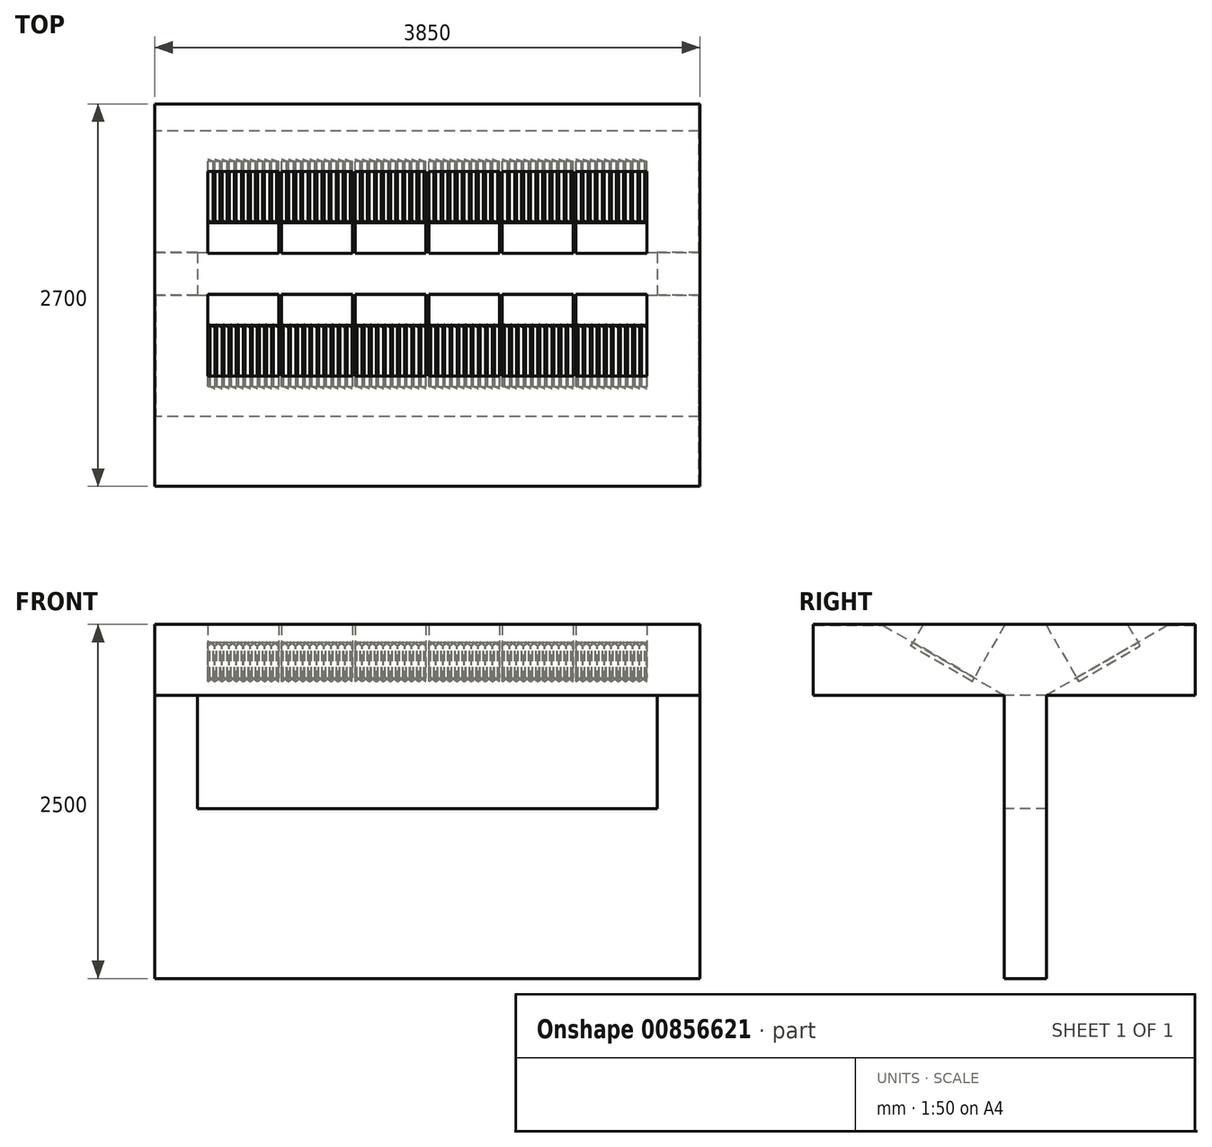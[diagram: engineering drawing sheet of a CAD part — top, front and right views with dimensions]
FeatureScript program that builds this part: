
annotation { "Feature Type Name" : "Feature", "Feature Type Description" : "" }
export const myFeature = defineFeature(function(context is Context, id is Id, definition is map)
    precondition{}
    {
        {
            var Q0;
            Q0=qCreatedBy(makeId("Top.planeOp"),FACE);
            var sketch = newSketch(context, id + "F0", { "sketchPlane" : qUnion([Q0])});
            skLineSegment(sketch, "E0.bottom", {"start": v(0, 0) * mm, "end": v(3850, 0) * mm});
            skLineSegment(sketch, "E0.top", {"start": v(0, -300) * mm, "end": v(3850, -300) * mm});
            skLineSegment(sketch, "E0.left", {"start": v(0, 0) * mm, "end": v(0, -300) * mm});
            skLineSegment(sketch, "E0.right", {"start": v(3850, 0) * mm, "end": v(3850, -300) * mm});
            skSolve(sketch);
        }
        {
            var Q0;
            Q0 = qSketchRegion(id + "F0", true);
            extrude(context, id + "F1", {"entities" : qUnion([Q0]), "depth" : 1200 * mm, "offsetDistance" : 25 * mm});
        }
        {
            var Q0;
            Q0=makeQuery(id+"F1.opExtrude","CAP_FACE",FACE,{"disambiguationData":[OSD([sQuery(id+"F0.wireOp",EDGE,"E0.bottom"),sQuery(id+"F0.wireOp",EDGE,"E0.top"),sQuery(id+"F0.wireOp",EDGE,"E0.left"),sQuery(id+"F0.wireOp",EDGE,"E0.right")])],"isStart":false});
            var sketch = newSketch(context, id + "F2", { "sketchPlane" : qUnion([Q0])});
            skLineSegment(sketch, "E1.bottom", {"start": v(0, 0) * mm, "end": v(300, 0) * mm});
            skLineSegment(sketch, "E1.top", {"start": v(0, -300) * mm, "end": v(300, -300) * mm});
            skLineSegment(sketch, "E1.left", {"start": v(0, 0) * mm, "end": v(0, -300) * mm});
            skLineSegment(sketch, "E1.right", {"start": v(300, 0) * mm, "end": v(300, -300) * mm});
            skLineSegment(sketch, "E2.bottom", {"start": v(3850, 0) * mm, "end": v(3550, 0) * mm});
            skLineSegment(sketch, "E2.top", {"start": v(3850, -300) * mm, "end": v(3550, -300) * mm});
            skLineSegment(sketch, "E2.left", {"start": v(3850, 0) * mm, "end": v(3850, -300) * mm});
            skLineSegment(sketch, "E2.right", {"start": v(3550, 0) * mm, "end": v(3550, -300) * mm});
            skSolve(sketch);
        }
        {
            var Q0;
            Q0 = qSketchRegion(id + "F2", true);
            extrude(context, id + "F3", {"entities" : qUnion([Q0]), "operationType" : NewBodyOperationType.ADD, "depth" : 800 * mm, "offsetDistance" : 25 * mm});
        }
        {
            var Q0;
            Q0=makeQuery(id+"F3.opExtrude","CAP_FACE",FACE,{"disambiguationData":[OSD([sQuery(id+"F2.wireOp",EDGE,"E1.bottom"),sQuery(id+"F2.wireOp",EDGE,"E1.top"),sQuery(id+"F2.wireOp",EDGE,"E1.left"),sQuery(id+"F2.wireOp",EDGE,"E1.right")])],"isStart":false});
            var sketch = newSketch(context, id + "F4", { "sketchPlane" : qUnion([Q0])});
            skLineSegment(sketch, "E3.bottom", {"start": v(0, 1050) * mm, "end": v(3850, 1050) * mm});
            skLineSegment(sketch, "E3.top", {"start": v(0, -1650) * mm, "end": v(3850, -1650) * mm});
            skLineSegment(sketch, "E3.left", {"start": v(0, 1050) * mm, "end": v(0, -1650) * mm});
            skLineSegment(sketch, "E3.right", {"start": v(3850, 1050) * mm, "end": v(3850, -1650) * mm});
            skSolve(sketch);
        }
        {
            var Q0;
            Q0 = qSketchRegion(id + "F4", true);
            extrude(context, id + "F5", {"entities" : qUnion([Q0]), "operationType" : NewBodyOperationType.ADD, "depth" : 500 * mm, "offsetDistance" : 25 * mm});
        }
        {
            var Q0;
            Q0=makeQuery(id+"F5.opExtrude","CAP_FACE",FACE,{"disambiguationData":[OSD([sQuery(id+"F4.wireOp",EDGE,"E3.bottom"),sQuery(id+"F4.wireOp",EDGE,"E3.top"),sQuery(id+"F4.wireOp",EDGE,"E3.left"),sQuery(id+"F4.wireOp",EDGE,"E3.right")])],"isStart":true});
            var sketch = newSketch(context, id + "F6", { "sketchPlane" : qUnion([Q0])});
            skLineSegment(sketch, "E4.bottom", {"start": v(5, 1645) * mm, "end": v(3845, 1645) * mm});
            skLineSegment(sketch, "E4.top", {"start": v(5, 300) * mm, "end": v(3845, 300) * mm});
            skLineSegment(sketch, "E4.left", {"start": v(5, 1645) * mm, "end": v(5, 300) * mm});
            skLineSegment(sketch, "E4.right", {"start": v(3845, 1645) * mm, "end": v(3845, 300) * mm});
            skLineSegment(sketch, "E5.bottom", {"start": v(5, 0) * mm, "end": v(3845, 0) * mm});
            skLineSegment(sketch, "E5.top", {"start": v(5, -1045) * mm, "end": v(3845, -1045) * mm});
            skLineSegment(sketch, "E5.left", {"start": v(5, 0) * mm, "end": v(5, -1045) * mm});
            skLineSegment(sketch, "E5.right", {"start": v(3845, 0) * mm, "end": v(3845, -1045) * mm});
            skSolve(sketch);
        }
        {
            var Q0;
            Q0 = qSketchRegion(id + "F6", true);
            extrude(context, id + "F7", {"entities" : qUnion([Q0]), "operationType" : NewBodyOperationType.REMOVE, "oppositeDirection" : true, "depth" : 495 * mm, "offsetDistance" : 25 * mm});
        }
        {
            var Q0;
            Q0=makeQuery(id+"F7.boolean.opBoolean","COPY",FACE,{"derivedFrom":makeQuery(id+"F7.opExtrude","SWEPT_FACE",FACE,{"disambiguationData":[OSD([sQuery(id+"F6.wireOp",EDGE,"E4.left")])]})});
            var sketch = newSketch(context, id + "F8", { "sketchPlane" : qUnion([Q0])});
            skLineSegment(sketch, "E6", {"start": v(-300, 2000) * mm, "end": v(-1157.37, 2495) * mm});
            skLineSegment(sketch, "E7", {"start": v(-1157.37, 2495) * mm, "end": v(-300, 2495) * mm});
            skLineSegment(sketch, "E8", {"start": v(-300, 2495) * mm, "end": v(-300, 2000) * mm});
            skSolve(sketch);
        }
        {
            var Q0;
            Q0 = qSketchRegion(id + "F8", true);
            extrude(context, id + "F9", {"entities" : qUnion([Q0]), "operationType" : NewBodyOperationType.ADD, "endBound" : BoundingType.UP_TO_NEXT, "depth" : 25 * mm, "offsetDistance" : 25 * mm});
        }
        {
            var Q0;
            Q0=makeQuery(id+"F7.boolean.opBoolean","COPY",FACE,{"derivedFrom":makeQuery(id+"F7.opExtrude","SWEPT_FACE",FACE,{"disambiguationData":[OSD([sQuery(id+"F6.wireOp",EDGE,"E5.left")])]})});
            var sketch = newSketch(context, id + "F10", { "sketchPlane" : qUnion([Q0])});
            skLineSegment(sketch, "E9", {"start": v(0, 2000) * mm, "end": v(857.37, 2495) * mm});
            skLineSegment(sketch, "E10", {"start": v(857.37, 2495) * mm, "end": v(0, 2495) * mm});
            skLineSegment(sketch, "E11", {"start": v(0, 2495) * mm, "end": v(0, 2000) * mm});
            skSolve(sketch);
        }
        {
            var Q0;
            Q0 = qSketchRegion(id + "F10", true);
            extrude(context, id + "F11", {"entities" : qUnion([Q0]), "operationType" : NewBodyOperationType.ADD, "endBound" : BoundingType.UP_TO_NEXT, "depth" : 25 * mm, "offsetDistance" : 25 * mm});
        }
        {
            var Q0;
            Q0=makeQuery(id+"F9.opExtrude","SWEPT_FACE",FACE,{"disambiguationData":[OSD([sQuery(id+"F8.wireOp",EDGE,"E6")])]});
            var sketch = newSketch(context, id + "F12", { "sketchPlane" : qUnion([Q0])});
            skLineSegment(sketch, "E12.bottom", {"start": v(375, 2004.8) * mm, "end": v(875, 2004.8) * mm});
            skLineSegment(sketch, "E12.top", {"start": v(375, 1504.8) * mm, "end": v(875, 1504.8) * mm});
            skLineSegment(sketch, "E12.left", {"start": v(375, 2004.8) * mm, "end": v(375, 1504.8) * mm});
            skLineSegment(sketch, "E12.right", {"start": v(875, 2004.8) * mm, "end": v(875, 1504.8) * mm});
            skLineSegment(sketch, "E13.bottom", {"start": v(895, 2004.8) * mm, "end": v(1395, 2004.8) * mm});
            skLineSegment(sketch, "E13.top", {"start": v(895, 1504.8) * mm, "end": v(1395, 1504.8) * mm});
            skLineSegment(sketch, "E13.left", {"start": v(895, 2004.8) * mm, "end": v(895, 1504.8) * mm});
            skLineSegment(sketch, "E13.right", {"start": v(1395, 2004.8) * mm, "end": v(1395, 1504.8) * mm});
            skLineSegment(sketch, "E14.bottom", {"start": v(1415, 2004.8) * mm, "end": v(1915, 2004.8) * mm});
            skLineSegment(sketch, "E14.top", {"start": v(1415, 1504.8) * mm, "end": v(1915, 1504.8) * mm});
            skLineSegment(sketch, "E14.left", {"start": v(1415, 2004.8) * mm, "end": v(1415, 1504.8) * mm});
            skLineSegment(sketch, "E14.right", {"start": v(1915, 2004.8) * mm, "end": v(1915, 1504.8) * mm});
            skLineSegment(sketch, "E15.bottom", {"start": v(1935, 2004.8) * mm, "end": v(2435, 2004.8) * mm});
            skLineSegment(sketch, "E15.top", {"start": v(1935, 1504.8) * mm, "end": v(2435, 1504.8) * mm});
            skLineSegment(sketch, "E15.left", {"start": v(1935, 2004.8) * mm, "end": v(1935, 1504.8) * mm});
            skLineSegment(sketch, "E15.right", {"start": v(2435, 2004.8) * mm, "end": v(2435, 1504.8) * mm});
            skLineSegment(sketch, "E16.bottom", {"start": v(2455, 2004.8) * mm, "end": v(2955, 2004.8) * mm});
            skLineSegment(sketch, "E16.top", {"start": v(2455, 1504.8) * mm, "end": v(2955, 1504.8) * mm});
            skLineSegment(sketch, "E16.left", {"start": v(2455, 2004.8) * mm, "end": v(2455, 1504.8) * mm});
            skLineSegment(sketch, "E16.right", {"start": v(2955, 2004.8) * mm, "end": v(2955, 1504.8) * mm});
            skLineSegment(sketch, "E17.bottom", {"start": v(2975, 2004.8) * mm, "end": v(3475, 2004.8) * mm});
            skLineSegment(sketch, "E17.top", {"start": v(2975, 1504.8) * mm, "end": v(3475, 1504.8) * mm});
            skLineSegment(sketch, "E17.left", {"start": v(2975, 2004.8) * mm, "end": v(2975, 1504.8) * mm});
            skLineSegment(sketch, "E17.right", {"start": v(3475, 2004.8) * mm, "end": v(3475, 1504.8) * mm});
            skSolve(sketch);
        }
        {
            var Q0;
            Q0 = qSketchRegion(id + "F12", true);
            extrude(context, id + "F13", {"entities" : qUnion([Q0]), "operationType" : NewBodyOperationType.REMOVE, "endBound" : BoundingType.UP_TO_NEXT, "oppositeDirection" : true, "depth" : 25 * mm, "offsetDistance" : 25 * mm});
        }
        {
            var Q0;
            Q0=makeQuery(id+"F11.opExtrude","SWEPT_FACE",FACE,{"disambiguationData":[OSD([sQuery(id+"F10.wireOp",EDGE,"E9")])]});
            var sketch = newSketch(context, id + "F14", { "sketchPlane" : qUnion([Q0])});
            skLineSegment(sketch, "E18.bottom", {"start": v(375, -1245) * mm, "end": v(875, -1245) * mm});
            skLineSegment(sketch, "E18.top", {"start": v(375, -1745) * mm, "end": v(875, -1745) * mm});
            skLineSegment(sketch, "E18.left", {"start": v(375, -1245) * mm, "end": v(375, -1745) * mm});
            skLineSegment(sketch, "E18.right", {"start": v(875, -1245) * mm, "end": v(875, -1745) * mm});
            skLineSegment(sketch, "E19.bottom", {"start": v(895, -1245) * mm, "end": v(1395, -1245) * mm});
            skLineSegment(sketch, "E19.top", {"start": v(895, -1745) * mm, "end": v(1395, -1745) * mm});
            skLineSegment(sketch, "E19.left", {"start": v(895, -1245) * mm, "end": v(895, -1745) * mm});
            skLineSegment(sketch, "E19.right", {"start": v(1395, -1245) * mm, "end": v(1395, -1745) * mm});
            skLineSegment(sketch, "E20.bottom", {"start": v(1415, -1245) * mm, "end": v(1915, -1245) * mm});
            skLineSegment(sketch, "E20.top", {"start": v(1415, -1745) * mm, "end": v(1915, -1745) * mm});
            skLineSegment(sketch, "E20.left", {"start": v(1415, -1245) * mm, "end": v(1415, -1745) * mm});
            skLineSegment(sketch, "E20.right", {"start": v(1915, -1245) * mm, "end": v(1915, -1745) * mm});
            skLineSegment(sketch, "E21.bottom", {"start": v(1935, -1245) * mm, "end": v(2435, -1245) * mm});
            skLineSegment(sketch, "E21.top", {"start": v(1935, -1745) * mm, "end": v(2435, -1745) * mm});
            skLineSegment(sketch, "E21.left", {"start": v(1935, -1245) * mm, "end": v(1935, -1745) * mm});
            skLineSegment(sketch, "E21.right", {"start": v(2435, -1245) * mm, "end": v(2435, -1745) * mm});
            skLineSegment(sketch, "E22.bottom", {"start": v(2455, -1245) * mm, "end": v(2955, -1245) * mm});
            skLineSegment(sketch, "E22.top", {"start": v(2455, -1745) * mm, "end": v(2955, -1745) * mm});
            skLineSegment(sketch, "E22.left", {"start": v(2455, -1245) * mm, "end": v(2455, -1745) * mm});
            skLineSegment(sketch, "E22.right", {"start": v(2955, -1245) * mm, "end": v(2955, -1745) * mm});
            skLineSegment(sketch, "E23.bottom", {"start": v(2975, -1245) * mm, "end": v(3475, -1245) * mm});
            skLineSegment(sketch, "E23.top", {"start": v(2975, -1745) * mm, "end": v(3475, -1745) * mm});
            skLineSegment(sketch, "E23.left", {"start": v(2975, -1245) * mm, "end": v(2975, -1745) * mm});
            skLineSegment(sketch, "E23.right", {"start": v(3475, -1245) * mm, "end": v(3475, -1745) * mm});
            skSolve(sketch);
        }
        {
            var Q0;
            Q0 = qSketchRegion(id + "F14", true);
            extrude(context, id + "F15", {"entities" : qUnion([Q0]), "operationType" : NewBodyOperationType.REMOVE, "endBound" : BoundingType.UP_TO_NEXT, "oppositeDirection" : true, "depth" : 25 * mm, "offsetDistance" : 25 * mm});
        }
        {
            var Q0;
            Q0=makeQuery(id+"F13.boolean.opBoolean","COPY",FACE,{"derivedFrom":makeQuery(id+"F13.opExtrude","SWEPT_FACE",FACE,{"disambiguationData":[OSD([sQuery(id+"F12.wireOp",EDGE,"E12.bottom")])]})});
            var sketch = newSketch(context, id + "F16", { "sketchPlane" : qUnion([Q0])});
            skLineSegment(sketch, "E24", {"start": v(-385, 1584.55) * mm, "end": v(-423.3, 1552.41) * mm});
            skLineSegment(sketch, "E25", {"start": v(-423.3, 1552.41) * mm, "end": v(-424.9, 1554.33) * mm});
            skLineSegment(sketch, "E26", {"start": v(-424.9, 1554.33) * mm, "end": v(-388.89, 1584.55) * mm});
            skLineSegment(sketch, "E27", {"start": v(-388.89, 1584.55) * mm, "end": v(-385, 1584.55) * mm});
            skLineSegment(sketch, "E28.1.0.0", {"start": v(-435, 1584.55) * mm, "end": v(-473.3, 1552.41) * mm});
            skLineSegment(sketch, "E28.1.0.1", {"start": v(-474.9, 1554.33) * mm, "end": v(-438.89, 1584.55) * mm});
            skLineSegment(sketch, "E28.1.0.2", {"start": v(-473.3, 1552.41) * mm, "end": v(-474.9, 1554.33) * mm});
            skLineSegment(sketch, "E28.1.0.3", {"start": v(-438.89, 1584.55) * mm, "end": v(-435, 1584.55) * mm});
            skLineSegment(sketch, "E28.2.0.0", {"start": v(-485, 1584.55) * mm, "end": v(-523.3, 1552.41) * mm});
            skLineSegment(sketch, "E28.2.0.1", {"start": v(-524.9, 1554.33) * mm, "end": v(-488.89, 1584.55) * mm});
            skLineSegment(sketch, "E28.2.0.2", {"start": v(-523.3, 1552.41) * mm, "end": v(-524.9, 1554.33) * mm});
            skLineSegment(sketch, "E28.2.0.3", {"start": v(-488.89, 1584.55) * mm, "end": v(-485, 1584.55) * mm});
            skLineSegment(sketch, "E28.3.0.0", {"start": v(-535, 1584.55) * mm, "end": v(-573.3, 1552.41) * mm});
            skLineSegment(sketch, "E28.3.0.1", {"start": v(-574.9, 1554.33) * mm, "end": v(-538.89, 1584.55) * mm});
            skLineSegment(sketch, "E28.3.0.2", {"start": v(-573.3, 1552.41) * mm, "end": v(-574.9, 1554.33) * mm});
            skLineSegment(sketch, "E28.3.0.3", {"start": v(-538.89, 1584.55) * mm, "end": v(-535, 1584.55) * mm});
            skLineSegment(sketch, "E28.4.0.0", {"start": v(-585, 1584.55) * mm, "end": v(-623.3, 1552.41) * mm});
            skLineSegment(sketch, "E28.4.0.1", {"start": v(-624.9, 1554.33) * mm, "end": v(-588.89, 1584.55) * mm});
            skLineSegment(sketch, "E28.4.0.2", {"start": v(-623.3, 1552.41) * mm, "end": v(-624.9, 1554.33) * mm});
            skLineSegment(sketch, "E28.4.0.3", {"start": v(-588.89, 1584.55) * mm, "end": v(-585, 1584.55) * mm});
            skLineSegment(sketch, "E28.5.0.0", {"start": v(-635, 1584.55) * mm, "end": v(-673.3, 1552.41) * mm});
            skLineSegment(sketch, "E28.5.0.1", {"start": v(-674.9, 1554.33) * mm, "end": v(-638.89, 1584.55) * mm});
            skLineSegment(sketch, "E28.5.0.2", {"start": v(-673.3, 1552.41) * mm, "end": v(-674.9, 1554.33) * mm});
            skLineSegment(sketch, "E28.5.0.3", {"start": v(-638.89, 1584.55) * mm, "end": v(-635, 1584.55) * mm});
            skLineSegment(sketch, "E28.6.0.0", {"start": v(-685, 1584.55) * mm, "end": v(-723.3, 1552.41) * mm});
            skLineSegment(sketch, "E28.6.0.1", {"start": v(-724.9, 1554.33) * mm, "end": v(-688.89, 1584.55) * mm});
            skLineSegment(sketch, "E28.6.0.2", {"start": v(-723.3, 1552.41) * mm, "end": v(-724.9, 1554.33) * mm});
            skLineSegment(sketch, "E28.6.0.3", {"start": v(-688.89, 1584.55) * mm, "end": v(-685, 1584.55) * mm});
            skLineSegment(sketch, "E28.7.0.0", {"start": v(-735, 1584.55) * mm, "end": v(-773.3, 1552.41) * mm});
            skLineSegment(sketch, "E28.7.0.1", {"start": v(-774.9, 1554.33) * mm, "end": v(-738.89, 1584.55) * mm});
            skLineSegment(sketch, "E28.7.0.2", {"start": v(-773.3, 1552.41) * mm, "end": v(-774.9, 1554.33) * mm});
            skLineSegment(sketch, "E28.7.0.3", {"start": v(-738.89, 1584.55) * mm, "end": v(-735, 1584.55) * mm});
            skLineSegment(sketch, "E28.8.0.0", {"start": v(-785, 1584.55) * mm, "end": v(-823.3, 1552.41) * mm});
            skLineSegment(sketch, "E28.8.0.1", {"start": v(-824.9, 1554.33) * mm, "end": v(-788.89, 1584.55) * mm});
            skLineSegment(sketch, "E28.8.0.2", {"start": v(-823.3, 1552.41) * mm, "end": v(-824.9, 1554.33) * mm});
            skLineSegment(sketch, "E28.8.0.3", {"start": v(-788.89, 1584.55) * mm, "end": v(-785, 1584.55) * mm});
            skLineSegment(sketch, "E28.9.0.0", {"start": v(-835, 1584.55) * mm, "end": v(-873.3, 1552.41) * mm});
            skLineSegment(sketch, "E28.9.0.1", {"start": v(-874.9, 1554.33) * mm, "end": v(-838.89, 1584.55) * mm});
            skLineSegment(sketch, "E28.9.0.2", {"start": v(-873.3, 1552.41) * mm, "end": v(-874.9, 1554.33) * mm});
            skLineSegment(sketch, "E28.9.0.3", {"start": v(-838.89, 1584.55) * mm, "end": v(-835, 1584.55) * mm});
            skLineSegment(sketch, "E28.direction1", {"start": v(-423.3, 1552.41) * mm, "end": v(-473.3, 1552.41) * mm, "construction": true});
            skLineSegment(sketch, "E29.1.0.0", {"start": v(-944.9, 1554.33) * mm, "end": v(-908.89, 1584.55) * mm});
            skLineSegment(sketch, "E29.1.0.1", {"start": v(-905, 1584.55) * mm, "end": v(-943.3, 1552.41) * mm});
            skLineSegment(sketch, "E29.1.0.2", {"start": v(-1394.9, 1554.33) * mm, "end": v(-1358.89, 1584.55) * mm});
            skLineSegment(sketch, "E29.1.0.3", {"start": v(-1194.9, 1554.33) * mm, "end": v(-1158.89, 1584.55) * mm});
            skLineSegment(sketch, "E29.1.0.4", {"start": v(-955, 1584.55) * mm, "end": v(-993.3, 1552.41) * mm});
            skLineSegment(sketch, "E29.1.0.5", {"start": v(-1355, 1584.55) * mm, "end": v(-1393.3, 1552.41) * mm});
            skLineSegment(sketch, "E29.1.0.6", {"start": v(-1294.9, 1554.33) * mm, "end": v(-1258.89, 1584.55) * mm});
            skLineSegment(sketch, "E29.1.0.7", {"start": v(-1155, 1584.55) * mm, "end": v(-1193.3, 1552.41) * mm});
            skLineSegment(sketch, "E29.1.0.8", {"start": v(-994.9, 1554.33) * mm, "end": v(-958.89, 1584.55) * mm});
            skLineSegment(sketch, "E29.1.0.9", {"start": v(-1344.9, 1554.33) * mm, "end": v(-1308.89, 1584.55) * mm});
            skLineSegment(sketch, "E29.1.0.10", {"start": v(-1144.9, 1554.33) * mm, "end": v(-1108.89, 1584.55) * mm});
            skLineSegment(sketch, "E29.1.0.11", {"start": v(-1305, 1584.55) * mm, "end": v(-1343.3, 1552.41) * mm});
            skLineSegment(sketch, "E29.1.0.12", {"start": v(-1105, 1584.55) * mm, "end": v(-1143.3, 1552.41) * mm});
            skLineSegment(sketch, "E29.1.0.13", {"start": v(-1005, 1584.55) * mm, "end": v(-1043.3, 1552.41) * mm});
            skLineSegment(sketch, "E29.1.0.14", {"start": v(-1255, 1584.55) * mm, "end": v(-1293.3, 1552.41) * mm});
            skLineSegment(sketch, "E29.1.0.15", {"start": v(-1044.9, 1554.33) * mm, "end": v(-1008.89, 1584.55) * mm});
            skLineSegment(sketch, "E29.1.0.16", {"start": v(-1094.9, 1554.33) * mm, "end": v(-1058.89, 1584.55) * mm});
            skLineSegment(sketch, "E29.1.0.17", {"start": v(-1244.9, 1554.33) * mm, "end": v(-1208.89, 1584.55) * mm});
            skLineSegment(sketch, "E29.1.0.18", {"start": v(-1055, 1584.55) * mm, "end": v(-1093.3, 1552.41) * mm});
            skLineSegment(sketch, "E29.1.0.19", {"start": v(-943.3, 1552.41) * mm, "end": v(-993.3, 1552.41) * mm, "construction": true});
            skLineSegment(sketch, "E29.1.0.20", {"start": v(-1205, 1584.55) * mm, "end": v(-1243.3, 1552.41) * mm});
            skLineSegment(sketch, "E29.1.0.21", {"start": v(-1393.3, 1552.41) * mm, "end": v(-1394.9, 1554.33) * mm});
            skLineSegment(sketch, "E29.1.0.22", {"start": v(-1193.3, 1552.41) * mm, "end": v(-1194.9, 1554.33) * mm});
            skLineSegment(sketch, "E29.1.0.23", {"start": v(-908.89, 1584.55) * mm, "end": v(-905, 1584.55) * mm});
            skLineSegment(sketch, "E29.1.0.24", {"start": v(-1293.3, 1552.41) * mm, "end": v(-1294.9, 1554.33) * mm});
            skLineSegment(sketch, "E29.1.0.25", {"start": v(-1258.89, 1584.55) * mm, "end": v(-1255, 1584.55) * mm});
            skLineSegment(sketch, "E29.1.0.26", {"start": v(-1308.89, 1584.55) * mm, "end": v(-1305, 1584.55) * mm});
            skLineSegment(sketch, "E29.1.0.27", {"start": v(-1108.89, 1584.55) * mm, "end": v(-1105, 1584.55) * mm});
            skLineSegment(sketch, "E29.1.0.28", {"start": v(-1343.3, 1552.41) * mm, "end": v(-1344.9, 1554.33) * mm});
            skLineSegment(sketch, "E29.1.0.29", {"start": v(-1143.3, 1552.41) * mm, "end": v(-1144.9, 1554.33) * mm});
            skLineSegment(sketch, "E29.1.0.30", {"start": v(-958.89, 1584.55) * mm, "end": v(-955, 1584.55) * mm});
            skLineSegment(sketch, "E29.1.0.31", {"start": v(-1208.89, 1584.55) * mm, "end": v(-1205, 1584.55) * mm});
            skLineSegment(sketch, "E29.1.0.32", {"start": v(-1058.89, 1584.55) * mm, "end": v(-1055, 1584.55) * mm});
            skLineSegment(sketch, "E29.1.0.33", {"start": v(-1043.3, 1552.41) * mm, "end": v(-1044.9, 1554.33) * mm});
            skLineSegment(sketch, "E29.1.0.34", {"start": v(-1243.3, 1552.41) * mm, "end": v(-1244.9, 1554.33) * mm});
            skLineSegment(sketch, "E29.1.0.35", {"start": v(-1008.89, 1584.55) * mm, "end": v(-1005, 1584.55) * mm});
            skLineSegment(sketch, "E29.1.0.36", {"start": v(-1093.3, 1552.41) * mm, "end": v(-1094.9, 1554.33) * mm});
            skLineSegment(sketch, "E29.1.0.37", {"start": v(-1358.89, 1584.55) * mm, "end": v(-1355, 1584.55) * mm});
            skLineSegment(sketch, "E29.1.0.38", {"start": v(-1158.89, 1584.55) * mm, "end": v(-1155, 1584.55) * mm});
            skLineSegment(sketch, "E29.1.0.39", {"start": v(-943.3, 1552.41) * mm, "end": v(-944.9, 1554.33) * mm});
            skLineSegment(sketch, "E29.1.0.40", {"start": v(-993.3, 1552.41) * mm, "end": v(-994.9, 1554.33) * mm});
            skLineSegment(sketch, "E29.2.0.0", {"start": v(-1464.9, 1554.33) * mm, "end": v(-1428.89, 1584.55) * mm});
            skLineSegment(sketch, "E29.2.0.1", {"start": v(-1425, 1584.55) * mm, "end": v(-1463.3, 1552.41) * mm});
            skLineSegment(sketch, "E29.2.0.2", {"start": v(-1914.9, 1554.33) * mm, "end": v(-1878.89, 1584.55) * mm});
            skLineSegment(sketch, "E29.2.0.3", {"start": v(-1714.9, 1554.33) * mm, "end": v(-1678.89, 1584.55) * mm});
            skLineSegment(sketch, "E29.2.0.4", {"start": v(-1475, 1584.55) * mm, "end": v(-1513.3, 1552.41) * mm});
            skLineSegment(sketch, "E29.2.0.5", {"start": v(-1875, 1584.55) * mm, "end": v(-1913.3, 1552.41) * mm});
            skLineSegment(sketch, "E29.2.0.6", {"start": v(-1814.9, 1554.33) * mm, "end": v(-1778.89, 1584.55) * mm});
            skLineSegment(sketch, "E29.2.0.7", {"start": v(-1675, 1584.55) * mm, "end": v(-1713.3, 1552.41) * mm});
            skLineSegment(sketch, "E29.2.0.8", {"start": v(-1514.9, 1554.33) * mm, "end": v(-1478.89, 1584.55) * mm});
            skLineSegment(sketch, "E29.2.0.9", {"start": v(-1864.9, 1554.33) * mm, "end": v(-1828.89, 1584.55) * mm});
            skLineSegment(sketch, "E29.2.0.10", {"start": v(-1664.9, 1554.33) * mm, "end": v(-1628.89, 1584.55) * mm});
            skLineSegment(sketch, "E29.2.0.11", {"start": v(-1825, 1584.55) * mm, "end": v(-1863.3, 1552.41) * mm});
            skLineSegment(sketch, "E29.2.0.12", {"start": v(-1625, 1584.55) * mm, "end": v(-1663.3, 1552.41) * mm});
            skLineSegment(sketch, "E29.2.0.13", {"start": v(-1525, 1584.55) * mm, "end": v(-1563.3, 1552.41) * mm});
            skLineSegment(sketch, "E29.2.0.14", {"start": v(-1775, 1584.55) * mm, "end": v(-1813.3, 1552.41) * mm});
            skLineSegment(sketch, "E29.2.0.15", {"start": v(-1564.9, 1554.33) * mm, "end": v(-1528.89, 1584.55) * mm});
            skLineSegment(sketch, "E29.2.0.16", {"start": v(-1614.9, 1554.33) * mm, "end": v(-1578.89, 1584.55) * mm});
            skLineSegment(sketch, "E29.2.0.17", {"start": v(-1764.9, 1554.33) * mm, "end": v(-1728.89, 1584.55) * mm});
            skLineSegment(sketch, "E29.2.0.18", {"start": v(-1575, 1584.55) * mm, "end": v(-1613.3, 1552.41) * mm});
            skLineSegment(sketch, "E29.2.0.19", {"start": v(-1463.3, 1552.41) * mm, "end": v(-1513.3, 1552.41) * mm, "construction": true});
            skLineSegment(sketch, "E29.2.0.20", {"start": v(-1725, 1584.55) * mm, "end": v(-1763.3, 1552.41) * mm});
            skLineSegment(sketch, "E29.2.0.21", {"start": v(-1913.3, 1552.41) * mm, "end": v(-1914.9, 1554.33) * mm});
            skLineSegment(sketch, "E29.2.0.22", {"start": v(-1713.3, 1552.41) * mm, "end": v(-1714.9, 1554.33) * mm});
            skLineSegment(sketch, "E29.2.0.23", {"start": v(-1428.89, 1584.55) * mm, "end": v(-1425, 1584.55) * mm});
            skLineSegment(sketch, "E29.2.0.24", {"start": v(-1813.3, 1552.41) * mm, "end": v(-1814.9, 1554.33) * mm});
            skLineSegment(sketch, "E29.2.0.25", {"start": v(-1778.89, 1584.55) * mm, "end": v(-1775, 1584.55) * mm});
            skLineSegment(sketch, "E29.2.0.26", {"start": v(-1828.89, 1584.55) * mm, "end": v(-1825, 1584.55) * mm});
            skLineSegment(sketch, "E29.2.0.27", {"start": v(-1628.89, 1584.55) * mm, "end": v(-1625, 1584.55) * mm});
            skLineSegment(sketch, "E29.2.0.28", {"start": v(-1863.3, 1552.41) * mm, "end": v(-1864.9, 1554.33) * mm});
            skLineSegment(sketch, "E29.2.0.29", {"start": v(-1663.3, 1552.41) * mm, "end": v(-1664.9, 1554.33) * mm});
            skLineSegment(sketch, "E29.2.0.30", {"start": v(-1478.89, 1584.55) * mm, "end": v(-1475, 1584.55) * mm});
            skLineSegment(sketch, "E29.2.0.31", {"start": v(-1728.89, 1584.55) * mm, "end": v(-1725, 1584.55) * mm});
            skLineSegment(sketch, "E29.2.0.32", {"start": v(-1578.89, 1584.55) * mm, "end": v(-1575, 1584.55) * mm});
            skLineSegment(sketch, "E29.2.0.33", {"start": v(-1563.3, 1552.41) * mm, "end": v(-1564.9, 1554.33) * mm});
            skLineSegment(sketch, "E29.2.0.34", {"start": v(-1763.3, 1552.41) * mm, "end": v(-1764.9, 1554.33) * mm});
            skLineSegment(sketch, "E29.2.0.35", {"start": v(-1528.89, 1584.55) * mm, "end": v(-1525, 1584.55) * mm});
            skLineSegment(sketch, "E29.2.0.36", {"start": v(-1613.3, 1552.41) * mm, "end": v(-1614.9, 1554.33) * mm});
            skLineSegment(sketch, "E29.2.0.37", {"start": v(-1878.89, 1584.55) * mm, "end": v(-1875, 1584.55) * mm});
            skLineSegment(sketch, "E29.2.0.38", {"start": v(-1678.89, 1584.55) * mm, "end": v(-1675, 1584.55) * mm});
            skLineSegment(sketch, "E29.2.0.39", {"start": v(-1463.3, 1552.41) * mm, "end": v(-1464.9, 1554.33) * mm});
            skLineSegment(sketch, "E29.2.0.40", {"start": v(-1513.3, 1552.41) * mm, "end": v(-1514.9, 1554.33) * mm});
            skLineSegment(sketch, "E29.3.0.0", {"start": v(-1984.9, 1554.33) * mm, "end": v(-1948.89, 1584.55) * mm});
            skLineSegment(sketch, "E29.3.0.1", {"start": v(-1945, 1584.55) * mm, "end": v(-1983.3, 1552.41) * mm});
            skLineSegment(sketch, "E29.3.0.2", {"start": v(-2434.9, 1554.33) * mm, "end": v(-2398.89, 1584.55) * mm});
            skLineSegment(sketch, "E29.3.0.3", {"start": v(-2234.9, 1554.33) * mm, "end": v(-2198.89, 1584.55) * mm});
            skLineSegment(sketch, "E29.3.0.4", {"start": v(-1995, 1584.55) * mm, "end": v(-2033.3, 1552.41) * mm});
            skLineSegment(sketch, "E29.3.0.5", {"start": v(-2395, 1584.55) * mm, "end": v(-2433.3, 1552.41) * mm});
            skLineSegment(sketch, "E29.3.0.6", {"start": v(-2334.9, 1554.33) * mm, "end": v(-2298.89, 1584.55) * mm});
            skLineSegment(sketch, "E29.3.0.7", {"start": v(-2195, 1584.55) * mm, "end": v(-2233.3, 1552.41) * mm});
            skLineSegment(sketch, "E29.3.0.8", {"start": v(-2034.9, 1554.33) * mm, "end": v(-1998.89, 1584.55) * mm});
            skLineSegment(sketch, "E29.3.0.9", {"start": v(-2384.9, 1554.33) * mm, "end": v(-2348.89, 1584.55) * mm});
            skLineSegment(sketch, "E29.3.0.10", {"start": v(-2184.9, 1554.33) * mm, "end": v(-2148.89, 1584.55) * mm});
            skLineSegment(sketch, "E29.3.0.11", {"start": v(-2345, 1584.55) * mm, "end": v(-2383.3, 1552.41) * mm});
            skLineSegment(sketch, "E29.3.0.12", {"start": v(-2145, 1584.55) * mm, "end": v(-2183.3, 1552.41) * mm});
            skLineSegment(sketch, "E29.3.0.13", {"start": v(-2045, 1584.55) * mm, "end": v(-2083.3, 1552.41) * mm});
            skLineSegment(sketch, "E29.3.0.14", {"start": v(-2295, 1584.55) * mm, "end": v(-2333.3, 1552.41) * mm});
            skLineSegment(sketch, "E29.3.0.15", {"start": v(-2084.9, 1554.33) * mm, "end": v(-2048.89, 1584.55) * mm});
            skLineSegment(sketch, "E29.3.0.16", {"start": v(-2134.9, 1554.33) * mm, "end": v(-2098.89, 1584.55) * mm});
            skLineSegment(sketch, "E29.3.0.17", {"start": v(-2284.9, 1554.33) * mm, "end": v(-2248.89, 1584.55) * mm});
            skLineSegment(sketch, "E29.3.0.18", {"start": v(-2095, 1584.55) * mm, "end": v(-2133.3, 1552.41) * mm});
            skLineSegment(sketch, "E29.3.0.19", {"start": v(-1983.3, 1552.41) * mm, "end": v(-2033.3, 1552.41) * mm, "construction": true});
            skLineSegment(sketch, "E29.3.0.20", {"start": v(-2245, 1584.55) * mm, "end": v(-2283.3, 1552.41) * mm});
            skLineSegment(sketch, "E29.3.0.21", {"start": v(-2433.3, 1552.41) * mm, "end": v(-2434.9, 1554.33) * mm});
            skLineSegment(sketch, "E29.3.0.22", {"start": v(-2233.3, 1552.41) * mm, "end": v(-2234.9, 1554.33) * mm});
            skLineSegment(sketch, "E29.3.0.23", {"start": v(-1948.89, 1584.55) * mm, "end": v(-1945, 1584.55) * mm});
            skLineSegment(sketch, "E29.3.0.24", {"start": v(-2333.3, 1552.41) * mm, "end": v(-2334.9, 1554.33) * mm});
            skLineSegment(sketch, "E29.3.0.25", {"start": v(-2298.89, 1584.55) * mm, "end": v(-2295, 1584.55) * mm});
            skLineSegment(sketch, "E29.3.0.26", {"start": v(-2348.89, 1584.55) * mm, "end": v(-2345, 1584.55) * mm});
            skLineSegment(sketch, "E29.3.0.27", {"start": v(-2148.89, 1584.55) * mm, "end": v(-2145, 1584.55) * mm});
            skLineSegment(sketch, "E29.3.0.28", {"start": v(-2383.3, 1552.41) * mm, "end": v(-2384.9, 1554.33) * mm});
            skLineSegment(sketch, "E29.3.0.29", {"start": v(-2183.3, 1552.41) * mm, "end": v(-2184.9, 1554.33) * mm});
            skLineSegment(sketch, "E29.3.0.30", {"start": v(-1998.89, 1584.55) * mm, "end": v(-1995, 1584.55) * mm});
            skLineSegment(sketch, "E29.3.0.31", {"start": v(-2248.89, 1584.55) * mm, "end": v(-2245, 1584.55) * mm});
            skLineSegment(sketch, "E29.3.0.32", {"start": v(-2098.89, 1584.55) * mm, "end": v(-2095, 1584.55) * mm});
            skLineSegment(sketch, "E29.3.0.33", {"start": v(-2083.3, 1552.41) * mm, "end": v(-2084.9, 1554.33) * mm});
            skLineSegment(sketch, "E29.3.0.34", {"start": v(-2283.3, 1552.41) * mm, "end": v(-2284.9, 1554.33) * mm});
            skLineSegment(sketch, "E29.3.0.35", {"start": v(-2048.89, 1584.55) * mm, "end": v(-2045, 1584.55) * mm});
            skLineSegment(sketch, "E29.3.0.36", {"start": v(-2133.3, 1552.41) * mm, "end": v(-2134.9, 1554.33) * mm});
            skLineSegment(sketch, "E29.3.0.37", {"start": v(-2398.89, 1584.55) * mm, "end": v(-2395, 1584.55) * mm});
            skLineSegment(sketch, "E29.3.0.38", {"start": v(-2198.89, 1584.55) * mm, "end": v(-2195, 1584.55) * mm});
            skLineSegment(sketch, "E29.3.0.39", {"start": v(-1983.3, 1552.41) * mm, "end": v(-1984.9, 1554.33) * mm});
            skLineSegment(sketch, "E29.3.0.40", {"start": v(-2033.3, 1552.41) * mm, "end": v(-2034.9, 1554.33) * mm});
            skLineSegment(sketch, "E29.4.0.0", {"start": v(-2504.9, 1554.33) * mm, "end": v(-2468.89, 1584.55) * mm});
            skLineSegment(sketch, "E29.4.0.1", {"start": v(-2465, 1584.55) * mm, "end": v(-2503.3, 1552.41) * mm});
            skLineSegment(sketch, "E29.4.0.2", {"start": v(-2954.9, 1554.33) * mm, "end": v(-2918.89, 1584.55) * mm});
            skLineSegment(sketch, "E29.4.0.3", {"start": v(-2754.9, 1554.33) * mm, "end": v(-2718.89, 1584.55) * mm});
            skLineSegment(sketch, "E29.4.0.4", {"start": v(-2515, 1584.55) * mm, "end": v(-2553.3, 1552.41) * mm});
            skLineSegment(sketch, "E29.4.0.5", {"start": v(-2915, 1584.55) * mm, "end": v(-2953.3, 1552.41) * mm});
            skLineSegment(sketch, "E29.4.0.6", {"start": v(-2854.9, 1554.33) * mm, "end": v(-2818.89, 1584.55) * mm});
            skLineSegment(sketch, "E29.4.0.7", {"start": v(-2715, 1584.55) * mm, "end": v(-2753.3, 1552.41) * mm});
            skLineSegment(sketch, "E29.4.0.8", {"start": v(-2554.9, 1554.33) * mm, "end": v(-2518.89, 1584.55) * mm});
            skLineSegment(sketch, "E29.4.0.9", {"start": v(-2904.9, 1554.33) * mm, "end": v(-2868.89, 1584.55) * mm});
            skLineSegment(sketch, "E29.4.0.10", {"start": v(-2704.9, 1554.33) * mm, "end": v(-2668.89, 1584.55) * mm});
            skLineSegment(sketch, "E29.4.0.11", {"start": v(-2865, 1584.55) * mm, "end": v(-2903.3, 1552.41) * mm});
            skLineSegment(sketch, "E29.4.0.12", {"start": v(-2665, 1584.55) * mm, "end": v(-2703.3, 1552.41) * mm});
            skLineSegment(sketch, "E29.4.0.13", {"start": v(-2565, 1584.55) * mm, "end": v(-2603.3, 1552.41) * mm});
            skLineSegment(sketch, "E29.4.0.14", {"start": v(-2815, 1584.55) * mm, "end": v(-2853.3, 1552.41) * mm});
            skLineSegment(sketch, "E29.4.0.15", {"start": v(-2604.9, 1554.33) * mm, "end": v(-2568.89, 1584.55) * mm});
            skLineSegment(sketch, "E29.4.0.16", {"start": v(-2654.9, 1554.33) * mm, "end": v(-2618.89, 1584.55) * mm});
            skLineSegment(sketch, "E29.4.0.17", {"start": v(-2804.9, 1554.33) * mm, "end": v(-2768.89, 1584.55) * mm});
            skLineSegment(sketch, "E29.4.0.18", {"start": v(-2615, 1584.55) * mm, "end": v(-2653.3, 1552.41) * mm});
            skLineSegment(sketch, "E29.4.0.19", {"start": v(-2503.3, 1552.41) * mm, "end": v(-2553.3, 1552.41) * mm, "construction": true});
            skLineSegment(sketch, "E29.4.0.20", {"start": v(-2765, 1584.55) * mm, "end": v(-2803.3, 1552.41) * mm});
            skLineSegment(sketch, "E29.4.0.21", {"start": v(-2953.3, 1552.41) * mm, "end": v(-2954.9, 1554.33) * mm});
            skLineSegment(sketch, "E29.4.0.22", {"start": v(-2753.3, 1552.41) * mm, "end": v(-2754.9, 1554.33) * mm});
            skLineSegment(sketch, "E29.4.0.23", {"start": v(-2468.89, 1584.55) * mm, "end": v(-2465, 1584.55) * mm});
            skLineSegment(sketch, "E29.4.0.24", {"start": v(-2853.3, 1552.41) * mm, "end": v(-2854.9, 1554.33) * mm});
            skLineSegment(sketch, "E29.4.0.25", {"start": v(-2818.89, 1584.55) * mm, "end": v(-2815, 1584.55) * mm});
            skLineSegment(sketch, "E29.4.0.26", {"start": v(-2868.89, 1584.55) * mm, "end": v(-2865, 1584.55) * mm});
            skLineSegment(sketch, "E29.4.0.27", {"start": v(-2668.89, 1584.55) * mm, "end": v(-2665, 1584.55) * mm});
            skLineSegment(sketch, "E29.4.0.28", {"start": v(-2903.3, 1552.41) * mm, "end": v(-2904.9, 1554.33) * mm});
            skLineSegment(sketch, "E29.4.0.29", {"start": v(-2703.3, 1552.41) * mm, "end": v(-2704.9, 1554.33) * mm});
            skLineSegment(sketch, "E29.4.0.30", {"start": v(-2518.89, 1584.55) * mm, "end": v(-2515, 1584.55) * mm});
            skLineSegment(sketch, "E29.4.0.31", {"start": v(-2768.89, 1584.55) * mm, "end": v(-2765, 1584.55) * mm});
            skLineSegment(sketch, "E29.4.0.32", {"start": v(-2618.89, 1584.55) * mm, "end": v(-2615, 1584.55) * mm});
            skLineSegment(sketch, "E29.4.0.33", {"start": v(-2603.3, 1552.41) * mm, "end": v(-2604.9, 1554.33) * mm});
            skLineSegment(sketch, "E29.4.0.34", {"start": v(-2803.3, 1552.41) * mm, "end": v(-2804.9, 1554.33) * mm});
            skLineSegment(sketch, "E29.4.0.35", {"start": v(-2568.89, 1584.55) * mm, "end": v(-2565, 1584.55) * mm});
            skLineSegment(sketch, "E29.4.0.36", {"start": v(-2653.3, 1552.41) * mm, "end": v(-2654.9, 1554.33) * mm});
            skLineSegment(sketch, "E29.4.0.37", {"start": v(-2918.89, 1584.55) * mm, "end": v(-2915, 1584.55) * mm});
            skLineSegment(sketch, "E29.4.0.38", {"start": v(-2718.89, 1584.55) * mm, "end": v(-2715, 1584.55) * mm});
            skLineSegment(sketch, "E29.4.0.39", {"start": v(-2503.3, 1552.41) * mm, "end": v(-2504.9, 1554.33) * mm});
            skLineSegment(sketch, "E29.4.0.40", {"start": v(-2553.3, 1552.41) * mm, "end": v(-2554.9, 1554.33) * mm});
            skLineSegment(sketch, "E29.5.0.0", {"start": v(-3024.9, 1554.33) * mm, "end": v(-2988.89, 1584.55) * mm});
            skLineSegment(sketch, "E29.5.0.1", {"start": v(-2985, 1584.55) * mm, "end": v(-3023.3, 1552.41) * mm});
            skLineSegment(sketch, "E29.5.0.2", {"start": v(-3474.9, 1554.33) * mm, "end": v(-3438.89, 1584.55) * mm});
            skLineSegment(sketch, "E29.5.0.3", {"start": v(-3274.9, 1554.33) * mm, "end": v(-3238.89, 1584.55) * mm});
            skLineSegment(sketch, "E29.5.0.4", {"start": v(-3035, 1584.55) * mm, "end": v(-3073.3, 1552.41) * mm});
            skLineSegment(sketch, "E29.5.0.5", {"start": v(-3435, 1584.55) * mm, "end": v(-3473.3, 1552.41) * mm});
            skLineSegment(sketch, "E29.5.0.6", {"start": v(-3374.9, 1554.33) * mm, "end": v(-3338.89, 1584.55) * mm});
            skLineSegment(sketch, "E29.5.0.7", {"start": v(-3235, 1584.55) * mm, "end": v(-3273.3, 1552.41) * mm});
            skLineSegment(sketch, "E29.5.0.8", {"start": v(-3074.9, 1554.33) * mm, "end": v(-3038.89, 1584.55) * mm});
            skLineSegment(sketch, "E29.5.0.9", {"start": v(-3424.9, 1554.33) * mm, "end": v(-3388.89, 1584.55) * mm});
            skLineSegment(sketch, "E29.5.0.10", {"start": v(-3224.9, 1554.33) * mm, "end": v(-3188.89, 1584.55) * mm});
            skLineSegment(sketch, "E29.5.0.11", {"start": v(-3385, 1584.55) * mm, "end": v(-3423.3, 1552.41) * mm});
            skLineSegment(sketch, "E29.5.0.12", {"start": v(-3185, 1584.55) * mm, "end": v(-3223.3, 1552.41) * mm});
            skLineSegment(sketch, "E29.5.0.13", {"start": v(-3085, 1584.55) * mm, "end": v(-3123.3, 1552.41) * mm});
            skLineSegment(sketch, "E29.5.0.14", {"start": v(-3335, 1584.55) * mm, "end": v(-3373.3, 1552.41) * mm});
            skLineSegment(sketch, "E29.5.0.15", {"start": v(-3124.9, 1554.33) * mm, "end": v(-3088.89, 1584.55) * mm});
            skLineSegment(sketch, "E29.5.0.16", {"start": v(-3174.9, 1554.33) * mm, "end": v(-3138.89, 1584.55) * mm});
            skLineSegment(sketch, "E29.5.0.17", {"start": v(-3324.9, 1554.33) * mm, "end": v(-3288.89, 1584.55) * mm});
            skLineSegment(sketch, "E29.5.0.18", {"start": v(-3135, 1584.55) * mm, "end": v(-3173.3, 1552.41) * mm});
            skLineSegment(sketch, "E29.5.0.19", {"start": v(-3023.3, 1552.41) * mm, "end": v(-3073.3, 1552.41) * mm, "construction": true});
            skLineSegment(sketch, "E29.5.0.20", {"start": v(-3285, 1584.55) * mm, "end": v(-3323.3, 1552.41) * mm});
            skLineSegment(sketch, "E29.5.0.21", {"start": v(-3473.3, 1552.41) * mm, "end": v(-3474.9, 1554.33) * mm});
            skLineSegment(sketch, "E29.5.0.22", {"start": v(-3273.3, 1552.41) * mm, "end": v(-3274.9, 1554.33) * mm});
            skLineSegment(sketch, "E29.5.0.23", {"start": v(-2988.89, 1584.55) * mm, "end": v(-2985, 1584.55) * mm});
            skLineSegment(sketch, "E29.5.0.24", {"start": v(-3373.3, 1552.41) * mm, "end": v(-3374.9, 1554.33) * mm});
            skLineSegment(sketch, "E29.5.0.25", {"start": v(-3338.89, 1584.55) * mm, "end": v(-3335, 1584.55) * mm});
            skLineSegment(sketch, "E29.5.0.26", {"start": v(-3388.89, 1584.55) * mm, "end": v(-3385, 1584.55) * mm});
            skLineSegment(sketch, "E29.5.0.27", {"start": v(-3188.89, 1584.55) * mm, "end": v(-3185, 1584.55) * mm});
            skLineSegment(sketch, "E29.5.0.28", {"start": v(-3423.3, 1552.41) * mm, "end": v(-3424.9, 1554.33) * mm});
            skLineSegment(sketch, "E29.5.0.29", {"start": v(-3223.3, 1552.41) * mm, "end": v(-3224.9, 1554.33) * mm});
            skLineSegment(sketch, "E29.5.0.30", {"start": v(-3038.89, 1584.55) * mm, "end": v(-3035, 1584.55) * mm});
            skLineSegment(sketch, "E29.5.0.31", {"start": v(-3288.89, 1584.55) * mm, "end": v(-3285, 1584.55) * mm});
            skLineSegment(sketch, "E29.5.0.32", {"start": v(-3138.89, 1584.55) * mm, "end": v(-3135, 1584.55) * mm});
            skLineSegment(sketch, "E29.5.0.33", {"start": v(-3123.3, 1552.41) * mm, "end": v(-3124.9, 1554.33) * mm});
            skLineSegment(sketch, "E29.5.0.34", {"start": v(-3323.3, 1552.41) * mm, "end": v(-3324.9, 1554.33) * mm});
            skLineSegment(sketch, "E29.5.0.35", {"start": v(-3088.89, 1584.55) * mm, "end": v(-3085, 1584.55) * mm});
            skLineSegment(sketch, "E29.5.0.36", {"start": v(-3173.3, 1552.41) * mm, "end": v(-3174.9, 1554.33) * mm});
            skLineSegment(sketch, "E29.5.0.37", {"start": v(-3438.89, 1584.55) * mm, "end": v(-3435, 1584.55) * mm});
            skLineSegment(sketch, "E29.5.0.38", {"start": v(-3238.89, 1584.55) * mm, "end": v(-3235, 1584.55) * mm});
            skLineSegment(sketch, "E29.5.0.39", {"start": v(-3023.3, 1552.41) * mm, "end": v(-3024.9, 1554.33) * mm});
            skLineSegment(sketch, "E29.5.0.40", {"start": v(-3073.3, 1552.41) * mm, "end": v(-3074.9, 1554.33) * mm});
            skLineSegment(sketch, "E29.direction1", {"start": v(-873.3, 1552.41) * mm, "end": v(-1393.3, 1552.41) * mm, "construction": true});
            skSolve(sketch);
        }
        {
            var Q0;
            Q0 = qSketchRegion(id + "F16", true);
            var Q1;
            Q1=makeQuery(id+"F13.boolean.opBoolean","COPY",FACE,{"derivedFrom":makeQuery(id+"F13.opExtrude","SWEPT_FACE",FACE,{"disambiguationData":[OSD([sQuery(id+"F12.wireOp",EDGE,"E12.top")])]})});
            extrude(context, id + "F17", {"entities" : qUnion([Q0]), "operationType" : NewBodyOperationType.ADD, "endBound" : BoundingType.UP_TO_SURFACE, "depth" : 25 * mm, "endBoundEntityFace" : qUnion([Q1]), "offsetDistance" : 25 * mm});
        }
        {
            var Q0;
            Q0=makeQuery(id+"F15.boolean.opBoolean","COPY",FACE,{"derivedFrom":makeQuery(id+"F15.opExtrude","SWEPT_FACE",FACE,{"disambiguationData":[OSD([sQuery(id+"F14.wireOp",EDGE,"E23.top")])]})});
            var sketch = newSketch(context, id + "F18", { "sketchPlane" : qUnion([Q0])});
            skLineSegment(sketch, "E30", {"start": v(3465, 1734.55) * mm, "end": v(3426.7, 1702.41) * mm});
            skLineSegment(sketch, "E31", {"start": v(3426.7, 1702.41) * mm, "end": v(3425.1, 1704.33) * mm});
            skLineSegment(sketch, "E32", {"start": v(3425.1, 1704.33) * mm, "end": v(3461.11, 1734.55) * mm});
            skLineSegment(sketch, "E33", {"start": v(3461.11, 1734.55) * mm, "end": v(3465, 1734.55) * mm});
            skLineSegment(sketch, "E34.1.0.0", {"start": v(3375.1, 1704.33) * mm, "end": v(3411.11, 1734.55) * mm});
            skLineSegment(sketch, "E34.1.0.1", {"start": v(3415, 1734.55) * mm, "end": v(3376.7, 1702.41) * mm});
            skLineSegment(sketch, "E34.1.0.2", {"start": v(3411.11, 1734.55) * mm, "end": v(3415, 1734.55) * mm});
            skLineSegment(sketch, "E34.1.0.3", {"start": v(3376.7, 1702.41) * mm, "end": v(3375.1, 1704.33) * mm});
            skLineSegment(sketch, "E34.2.0.0", {"start": v(3325.1, 1704.33) * mm, "end": v(3361.11, 1734.55) * mm});
            skLineSegment(sketch, "E34.2.0.1", {"start": v(3365, 1734.55) * mm, "end": v(3326.7, 1702.41) * mm});
            skLineSegment(sketch, "E34.2.0.2", {"start": v(3361.11, 1734.55) * mm, "end": v(3365, 1734.55) * mm});
            skLineSegment(sketch, "E34.2.0.3", {"start": v(3326.7, 1702.41) * mm, "end": v(3325.1, 1704.33) * mm});
            skLineSegment(sketch, "E34.3.0.0", {"start": v(3275.1, 1704.33) * mm, "end": v(3311.11, 1734.55) * mm});
            skLineSegment(sketch, "E34.3.0.1", {"start": v(3315, 1734.55) * mm, "end": v(3276.7, 1702.41) * mm});
            skLineSegment(sketch, "E34.3.0.2", {"start": v(3311.11, 1734.55) * mm, "end": v(3315, 1734.55) * mm});
            skLineSegment(sketch, "E34.3.0.3", {"start": v(3276.7, 1702.41) * mm, "end": v(3275.1, 1704.33) * mm});
            skLineSegment(sketch, "E34.4.0.0", {"start": v(3225.1, 1704.33) * mm, "end": v(3261.11, 1734.55) * mm});
            skLineSegment(sketch, "E34.4.0.1", {"start": v(3265, 1734.55) * mm, "end": v(3226.7, 1702.41) * mm});
            skLineSegment(sketch, "E34.4.0.2", {"start": v(3261.11, 1734.55) * mm, "end": v(3265, 1734.55) * mm});
            skLineSegment(sketch, "E34.4.0.3", {"start": v(3226.7, 1702.41) * mm, "end": v(3225.1, 1704.33) * mm});
            skLineSegment(sketch, "E34.5.0.0", {"start": v(3175.1, 1704.33) * mm, "end": v(3211.11, 1734.55) * mm});
            skLineSegment(sketch, "E34.5.0.1", {"start": v(3215, 1734.55) * mm, "end": v(3176.7, 1702.41) * mm});
            skLineSegment(sketch, "E34.5.0.2", {"start": v(3211.11, 1734.55) * mm, "end": v(3215, 1734.55) * mm});
            skLineSegment(sketch, "E34.5.0.3", {"start": v(3176.7, 1702.41) * mm, "end": v(3175.1, 1704.33) * mm});
            skLineSegment(sketch, "E34.6.0.0", {"start": v(3125.1, 1704.33) * mm, "end": v(3161.11, 1734.55) * mm});
            skLineSegment(sketch, "E34.6.0.1", {"start": v(3165, 1734.55) * mm, "end": v(3126.7, 1702.41) * mm});
            skLineSegment(sketch, "E34.6.0.2", {"start": v(3161.11, 1734.55) * mm, "end": v(3165, 1734.55) * mm});
            skLineSegment(sketch, "E34.6.0.3", {"start": v(3126.7, 1702.41) * mm, "end": v(3125.1, 1704.33) * mm});
            skLineSegment(sketch, "E34.7.0.0", {"start": v(3075.1, 1704.33) * mm, "end": v(3111.11, 1734.55) * mm});
            skLineSegment(sketch, "E34.7.0.1", {"start": v(3115, 1734.55) * mm, "end": v(3076.7, 1702.41) * mm});
            skLineSegment(sketch, "E34.7.0.2", {"start": v(3111.11, 1734.55) * mm, "end": v(3115, 1734.55) * mm});
            skLineSegment(sketch, "E34.7.0.3", {"start": v(3076.7, 1702.41) * mm, "end": v(3075.1, 1704.33) * mm});
            skLineSegment(sketch, "E34.8.0.0", {"start": v(3025.1, 1704.33) * mm, "end": v(3061.11, 1734.55) * mm});
            skLineSegment(sketch, "E34.8.0.1", {"start": v(3065, 1734.55) * mm, "end": v(3026.7, 1702.41) * mm});
            skLineSegment(sketch, "E34.8.0.2", {"start": v(3061.11, 1734.55) * mm, "end": v(3065, 1734.55) * mm});
            skLineSegment(sketch, "E34.8.0.3", {"start": v(3026.7, 1702.41) * mm, "end": v(3025.1, 1704.33) * mm});
            skLineSegment(sketch, "E34.9.0.0", {"start": v(2975.1, 1704.33) * mm, "end": v(3011.11, 1734.55) * mm});
            skLineSegment(sketch, "E34.9.0.1", {"start": v(3015, 1734.55) * mm, "end": v(2976.7, 1702.41) * mm});
            skLineSegment(sketch, "E34.9.0.2", {"start": v(3011.11, 1734.55) * mm, "end": v(3015, 1734.55) * mm});
            skLineSegment(sketch, "E34.9.0.3", {"start": v(2976.7, 1702.41) * mm, "end": v(2975.1, 1704.33) * mm});
            skLineSegment(sketch, "E34.direction1", {"start": v(3426.7, 1702.41) * mm, "end": v(3376.7, 1702.41) * mm, "construction": true});
            skLineSegment(sketch, "E35.1.0.0", {"start": v(2845, 1734.55) * mm, "end": v(2806.7, 1702.41) * mm});
            skLineSegment(sketch, "E35.1.0.1", {"start": v(2645, 1734.55) * mm, "end": v(2606.7, 1702.41) * mm});
            skLineSegment(sketch, "E35.1.0.2", {"start": v(2505.1, 1704.33) * mm, "end": v(2541.11, 1734.55) * mm});
            skLineSegment(sketch, "E35.1.0.3", {"start": v(2795, 1734.55) * mm, "end": v(2756.7, 1702.41) * mm});
            skLineSegment(sketch, "E35.1.0.4", {"start": v(2695, 1734.55) * mm, "end": v(2656.7, 1702.41) * mm});
            skLineSegment(sketch, "E35.1.0.5", {"start": v(2495, 1734.55) * mm, "end": v(2456.7, 1702.41) * mm});
            skLineSegment(sketch, "E35.1.0.6", {"start": v(2755.1, 1704.33) * mm, "end": v(2791.11, 1734.55) * mm});
            skLineSegment(sketch, "E35.1.0.7", {"start": v(2455.1, 1704.33) * mm, "end": v(2491.11, 1734.55) * mm});
            skLineSegment(sketch, "E35.1.0.8", {"start": v(2745, 1734.55) * mm, "end": v(2706.7, 1702.41) * mm});
            skLineSegment(sketch, "E35.1.0.9", {"start": v(2595, 1734.55) * mm, "end": v(2556.7, 1702.41) * mm});
            skLineSegment(sketch, "E35.1.0.10", {"start": v(2605.1, 1704.33) * mm, "end": v(2641.11, 1734.55) * mm});
            skLineSegment(sketch, "E35.1.0.11", {"start": v(2805.1, 1704.33) * mm, "end": v(2841.11, 1734.55) * mm});
            skLineSegment(sketch, "E35.1.0.12", {"start": v(2555.1, 1704.33) * mm, "end": v(2591.11, 1734.55) * mm});
            skLineSegment(sketch, "E35.1.0.13", {"start": v(2655.1, 1704.33) * mm, "end": v(2691.11, 1734.55) * mm});
            skLineSegment(sketch, "E35.1.0.14", {"start": v(2906.7, 1702.41) * mm, "end": v(2856.7, 1702.41) * mm, "construction": true});
            skLineSegment(sketch, "E35.1.0.15", {"start": v(2545, 1734.55) * mm, "end": v(2506.7, 1702.41) * mm});
            skLineSegment(sketch, "E35.1.0.16", {"start": v(2705.1, 1704.33) * mm, "end": v(2741.11, 1734.55) * mm});
            skLineSegment(sketch, "E35.1.0.17", {"start": v(2855.1, 1704.33) * mm, "end": v(2891.11, 1734.55) * mm});
            skLineSegment(sketch, "E35.1.0.18", {"start": v(2905.1, 1704.33) * mm, "end": v(2941.11, 1734.55) * mm});
            skLineSegment(sketch, "E35.1.0.19", {"start": v(2945, 1734.55) * mm, "end": v(2906.7, 1702.41) * mm});
            skLineSegment(sketch, "E35.1.0.20", {"start": v(2895, 1734.55) * mm, "end": v(2856.7, 1702.41) * mm});
            skLineSegment(sketch, "E35.1.0.21", {"start": v(2556.7, 1702.41) * mm, "end": v(2555.1, 1704.33) * mm});
            skLineSegment(sketch, "E35.1.0.22", {"start": v(2491.11, 1734.55) * mm, "end": v(2495, 1734.55) * mm});
            skLineSegment(sketch, "E35.1.0.23", {"start": v(2941.11, 1734.55) * mm, "end": v(2945, 1734.55) * mm});
            skLineSegment(sketch, "E35.1.0.24", {"start": v(2841.11, 1734.55) * mm, "end": v(2845, 1734.55) * mm});
            skLineSegment(sketch, "E35.1.0.25", {"start": v(2506.7, 1702.41) * mm, "end": v(2505.1, 1704.33) * mm});
            skLineSegment(sketch, "E35.1.0.26", {"start": v(2741.11, 1734.55) * mm, "end": v(2745, 1734.55) * mm});
            skLineSegment(sketch, "E35.1.0.27", {"start": v(2891.11, 1734.55) * mm, "end": v(2895, 1734.55) * mm});
            skLineSegment(sketch, "E35.1.0.28", {"start": v(2591.11, 1734.55) * mm, "end": v(2595, 1734.55) * mm});
            skLineSegment(sketch, "E35.1.0.29", {"start": v(2606.7, 1702.41) * mm, "end": v(2605.1, 1704.33) * mm});
            skLineSegment(sketch, "E35.1.0.30", {"start": v(2541.11, 1734.55) * mm, "end": v(2545, 1734.55) * mm});
            skLineSegment(sketch, "E35.1.0.31", {"start": v(2456.7, 1702.41) * mm, "end": v(2455.1, 1704.33) * mm});
            skLineSegment(sketch, "E35.1.0.32", {"start": v(2656.7, 1702.41) * mm, "end": v(2655.1, 1704.33) * mm});
            skLineSegment(sketch, "E35.1.0.33", {"start": v(2691.11, 1734.55) * mm, "end": v(2695, 1734.55) * mm});
            skLineSegment(sketch, "E35.1.0.34", {"start": v(2641.11, 1734.55) * mm, "end": v(2645, 1734.55) * mm});
            skLineSegment(sketch, "E35.1.0.35", {"start": v(2906.7, 1702.41) * mm, "end": v(2905.1, 1704.33) * mm});
            skLineSegment(sketch, "E35.1.0.36", {"start": v(2856.7, 1702.41) * mm, "end": v(2855.1, 1704.33) * mm});
            skLineSegment(sketch, "E35.1.0.37", {"start": v(2791.11, 1734.55) * mm, "end": v(2795, 1734.55) * mm});
            skLineSegment(sketch, "E35.1.0.38", {"start": v(2756.7, 1702.41) * mm, "end": v(2755.1, 1704.33) * mm});
            skLineSegment(sketch, "E35.1.0.39", {"start": v(2706.7, 1702.41) * mm, "end": v(2705.1, 1704.33) * mm});
            skLineSegment(sketch, "E35.1.0.40", {"start": v(2806.7, 1702.41) * mm, "end": v(2805.1, 1704.33) * mm});
            skLineSegment(sketch, "E35.2.0.0", {"start": v(2325, 1734.55) * mm, "end": v(2286.7, 1702.41) * mm});
            skLineSegment(sketch, "E35.2.0.1", {"start": v(2125, 1734.55) * mm, "end": v(2086.7, 1702.41) * mm});
            skLineSegment(sketch, "E35.2.0.2", {"start": v(1985.1, 1704.33) * mm, "end": v(2021.11, 1734.55) * mm});
            skLineSegment(sketch, "E35.2.0.3", {"start": v(2275, 1734.55) * mm, "end": v(2236.7, 1702.41) * mm});
            skLineSegment(sketch, "E35.2.0.4", {"start": v(2175, 1734.55) * mm, "end": v(2136.7, 1702.41) * mm});
            skLineSegment(sketch, "E35.2.0.5", {"start": v(1975, 1734.55) * mm, "end": v(1936.7, 1702.41) * mm});
            skLineSegment(sketch, "E35.2.0.6", {"start": v(2235.1, 1704.33) * mm, "end": v(2271.11, 1734.55) * mm});
            skLineSegment(sketch, "E35.2.0.7", {"start": v(1935.1, 1704.33) * mm, "end": v(1971.11, 1734.55) * mm});
            skLineSegment(sketch, "E35.2.0.8", {"start": v(2225, 1734.55) * mm, "end": v(2186.7, 1702.41) * mm});
            skLineSegment(sketch, "E35.2.0.9", {"start": v(2075, 1734.55) * mm, "end": v(2036.7, 1702.41) * mm});
            skLineSegment(sketch, "E35.2.0.10", {"start": v(2085.1, 1704.33) * mm, "end": v(2121.11, 1734.55) * mm});
            skLineSegment(sketch, "E35.2.0.11", {"start": v(2285.1, 1704.33) * mm, "end": v(2321.11, 1734.55) * mm});
            skLineSegment(sketch, "E35.2.0.12", {"start": v(2035.1, 1704.33) * mm, "end": v(2071.11, 1734.55) * mm});
            skLineSegment(sketch, "E35.2.0.13", {"start": v(2135.1, 1704.33) * mm, "end": v(2171.11, 1734.55) * mm});
            skLineSegment(sketch, "E35.2.0.14", {"start": v(2386.7, 1702.41) * mm, "end": v(2336.7, 1702.41) * mm, "construction": true});
            skLineSegment(sketch, "E35.2.0.15", {"start": v(2025, 1734.55) * mm, "end": v(1986.7, 1702.41) * mm});
            skLineSegment(sketch, "E35.2.0.16", {"start": v(2185.1, 1704.33) * mm, "end": v(2221.11, 1734.55) * mm});
            skLineSegment(sketch, "E35.2.0.17", {"start": v(2335.1, 1704.33) * mm, "end": v(2371.11, 1734.55) * mm});
            skLineSegment(sketch, "E35.2.0.18", {"start": v(2385.1, 1704.33) * mm, "end": v(2421.11, 1734.55) * mm});
            skLineSegment(sketch, "E35.2.0.19", {"start": v(2425, 1734.55) * mm, "end": v(2386.7, 1702.41) * mm});
            skLineSegment(sketch, "E35.2.0.20", {"start": v(2375, 1734.55) * mm, "end": v(2336.7, 1702.41) * mm});
            skLineSegment(sketch, "E35.2.0.21", {"start": v(2036.7, 1702.41) * mm, "end": v(2035.1, 1704.33) * mm});
            skLineSegment(sketch, "E35.2.0.22", {"start": v(1971.11, 1734.55) * mm, "end": v(1975, 1734.55) * mm});
            skLineSegment(sketch, "E35.2.0.23", {"start": v(2421.11, 1734.55) * mm, "end": v(2425, 1734.55) * mm});
            skLineSegment(sketch, "E35.2.0.24", {"start": v(2321.11, 1734.55) * mm, "end": v(2325, 1734.55) * mm});
            skLineSegment(sketch, "E35.2.0.25", {"start": v(1986.7, 1702.41) * mm, "end": v(1985.1, 1704.33) * mm});
            skLineSegment(sketch, "E35.2.0.26", {"start": v(2221.11, 1734.55) * mm, "end": v(2225, 1734.55) * mm});
            skLineSegment(sketch, "E35.2.0.27", {"start": v(2371.11, 1734.55) * mm, "end": v(2375, 1734.55) * mm});
            skLineSegment(sketch, "E35.2.0.28", {"start": v(2071.11, 1734.55) * mm, "end": v(2075, 1734.55) * mm});
            skLineSegment(sketch, "E35.2.0.29", {"start": v(2086.7, 1702.41) * mm, "end": v(2085.1, 1704.33) * mm});
            skLineSegment(sketch, "E35.2.0.30", {"start": v(2021.11, 1734.55) * mm, "end": v(2025, 1734.55) * mm});
            skLineSegment(sketch, "E35.2.0.31", {"start": v(1936.7, 1702.41) * mm, "end": v(1935.1, 1704.33) * mm});
            skLineSegment(sketch, "E35.2.0.32", {"start": v(2136.7, 1702.41) * mm, "end": v(2135.1, 1704.33) * mm});
            skLineSegment(sketch, "E35.2.0.33", {"start": v(2171.11, 1734.55) * mm, "end": v(2175, 1734.55) * mm});
            skLineSegment(sketch, "E35.2.0.34", {"start": v(2121.11, 1734.55) * mm, "end": v(2125, 1734.55) * mm});
            skLineSegment(sketch, "E35.2.0.35", {"start": v(2386.7, 1702.41) * mm, "end": v(2385.1, 1704.33) * mm});
            skLineSegment(sketch, "E35.2.0.36", {"start": v(2336.7, 1702.41) * mm, "end": v(2335.1, 1704.33) * mm});
            skLineSegment(sketch, "E35.2.0.37", {"start": v(2271.11, 1734.55) * mm, "end": v(2275, 1734.55) * mm});
            skLineSegment(sketch, "E35.2.0.38", {"start": v(2236.7, 1702.41) * mm, "end": v(2235.1, 1704.33) * mm});
            skLineSegment(sketch, "E35.2.0.39", {"start": v(2186.7, 1702.41) * mm, "end": v(2185.1, 1704.33) * mm});
            skLineSegment(sketch, "E35.2.0.40", {"start": v(2286.7, 1702.41) * mm, "end": v(2285.1, 1704.33) * mm});
            skLineSegment(sketch, "E35.3.0.0", {"start": v(1805, 1734.55) * mm, "end": v(1766.7, 1702.41) * mm});
            skLineSegment(sketch, "E35.3.0.1", {"start": v(1605, 1734.55) * mm, "end": v(1566.7, 1702.41) * mm});
            skLineSegment(sketch, "E35.3.0.2", {"start": v(1465.1, 1704.33) * mm, "end": v(1501.11, 1734.55) * mm});
            skLineSegment(sketch, "E35.3.0.3", {"start": v(1755, 1734.55) * mm, "end": v(1716.7, 1702.41) * mm});
            skLineSegment(sketch, "E35.3.0.4", {"start": v(1655, 1734.55) * mm, "end": v(1616.7, 1702.41) * mm});
            skLineSegment(sketch, "E35.3.0.5", {"start": v(1455, 1734.55) * mm, "end": v(1416.7, 1702.41) * mm});
            skLineSegment(sketch, "E35.3.0.6", {"start": v(1715.1, 1704.33) * mm, "end": v(1751.11, 1734.55) * mm});
            skLineSegment(sketch, "E35.3.0.7", {"start": v(1415.1, 1704.33) * mm, "end": v(1451.11, 1734.55) * mm});
            skLineSegment(sketch, "E35.3.0.8", {"start": v(1705, 1734.55) * mm, "end": v(1666.7, 1702.41) * mm});
            skLineSegment(sketch, "E35.3.0.9", {"start": v(1555, 1734.55) * mm, "end": v(1516.7, 1702.41) * mm});
            skLineSegment(sketch, "E35.3.0.10", {"start": v(1565.1, 1704.33) * mm, "end": v(1601.11, 1734.55) * mm});
            skLineSegment(sketch, "E35.3.0.11", {"start": v(1765.1, 1704.33) * mm, "end": v(1801.11, 1734.55) * mm});
            skLineSegment(sketch, "E35.3.0.12", {"start": v(1515.1, 1704.33) * mm, "end": v(1551.11, 1734.55) * mm});
            skLineSegment(sketch, "E35.3.0.13", {"start": v(1615.1, 1704.33) * mm, "end": v(1651.11, 1734.55) * mm});
            skLineSegment(sketch, "E35.3.0.14", {"start": v(1866.7, 1702.41) * mm, "end": v(1816.7, 1702.41) * mm, "construction": true});
            skLineSegment(sketch, "E35.3.0.15", {"start": v(1505, 1734.55) * mm, "end": v(1466.7, 1702.41) * mm});
            skLineSegment(sketch, "E35.3.0.16", {"start": v(1665.1, 1704.33) * mm, "end": v(1701.11, 1734.55) * mm});
            skLineSegment(sketch, "E35.3.0.17", {"start": v(1815.1, 1704.33) * mm, "end": v(1851.11, 1734.55) * mm});
            skLineSegment(sketch, "E35.3.0.18", {"start": v(1865.1, 1704.33) * mm, "end": v(1901.11, 1734.55) * mm});
            skLineSegment(sketch, "E35.3.0.19", {"start": v(1905, 1734.55) * mm, "end": v(1866.7, 1702.41) * mm});
            skLineSegment(sketch, "E35.3.0.20", {"start": v(1855, 1734.55) * mm, "end": v(1816.7, 1702.41) * mm});
            skLineSegment(sketch, "E35.3.0.21", {"start": v(1516.7, 1702.41) * mm, "end": v(1515.1, 1704.33) * mm});
            skLineSegment(sketch, "E35.3.0.22", {"start": v(1451.11, 1734.55) * mm, "end": v(1455, 1734.55) * mm});
            skLineSegment(sketch, "E35.3.0.23", {"start": v(1901.11, 1734.55) * mm, "end": v(1905, 1734.55) * mm});
            skLineSegment(sketch, "E35.3.0.24", {"start": v(1801.11, 1734.55) * mm, "end": v(1805, 1734.55) * mm});
            skLineSegment(sketch, "E35.3.0.25", {"start": v(1466.7, 1702.41) * mm, "end": v(1465.1, 1704.33) * mm});
            skLineSegment(sketch, "E35.3.0.26", {"start": v(1701.11, 1734.55) * mm, "end": v(1705, 1734.55) * mm});
            skLineSegment(sketch, "E35.3.0.27", {"start": v(1851.11, 1734.55) * mm, "end": v(1855, 1734.55) * mm});
            skLineSegment(sketch, "E35.3.0.28", {"start": v(1551.11, 1734.55) * mm, "end": v(1555, 1734.55) * mm});
            skLineSegment(sketch, "E35.3.0.29", {"start": v(1566.7, 1702.41) * mm, "end": v(1565.1, 1704.33) * mm});
            skLineSegment(sketch, "E35.3.0.30", {"start": v(1501.11, 1734.55) * mm, "end": v(1505, 1734.55) * mm});
            skLineSegment(sketch, "E35.3.0.31", {"start": v(1416.7, 1702.41) * mm, "end": v(1415.1, 1704.33) * mm});
            skLineSegment(sketch, "E35.3.0.32", {"start": v(1616.7, 1702.41) * mm, "end": v(1615.1, 1704.33) * mm});
            skLineSegment(sketch, "E35.3.0.33", {"start": v(1651.11, 1734.55) * mm, "end": v(1655, 1734.55) * mm});
            skLineSegment(sketch, "E35.3.0.34", {"start": v(1601.11, 1734.55) * mm, "end": v(1605, 1734.55) * mm});
            skLineSegment(sketch, "E35.3.0.35", {"start": v(1866.7, 1702.41) * mm, "end": v(1865.1, 1704.33) * mm});
            skLineSegment(sketch, "E35.3.0.36", {"start": v(1816.7, 1702.41) * mm, "end": v(1815.1, 1704.33) * mm});
            skLineSegment(sketch, "E35.3.0.37", {"start": v(1751.11, 1734.55) * mm, "end": v(1755, 1734.55) * mm});
            skLineSegment(sketch, "E35.3.0.38", {"start": v(1716.7, 1702.41) * mm, "end": v(1715.1, 1704.33) * mm});
            skLineSegment(sketch, "E35.3.0.39", {"start": v(1666.7, 1702.41) * mm, "end": v(1665.1, 1704.33) * mm});
            skLineSegment(sketch, "E35.3.0.40", {"start": v(1766.7, 1702.41) * mm, "end": v(1765.1, 1704.33) * mm});
            skLineSegment(sketch, "E35.4.0.0", {"start": v(1285, 1734.55) * mm, "end": v(1246.7, 1702.41) * mm});
            skLineSegment(sketch, "E35.4.0.1", {"start": v(1085, 1734.55) * mm, "end": v(1046.7, 1702.41) * mm});
            skLineSegment(sketch, "E35.4.0.2", {"start": v(945.1, 1704.33) * mm, "end": v(981.11, 1734.55) * mm});
            skLineSegment(sketch, "E35.4.0.3", {"start": v(1235, 1734.55) * mm, "end": v(1196.7, 1702.41) * mm});
            skLineSegment(sketch, "E35.4.0.4", {"start": v(1135, 1734.55) * mm, "end": v(1096.7, 1702.41) * mm});
            skLineSegment(sketch, "E35.4.0.5", {"start": v(935, 1734.55) * mm, "end": v(896.7, 1702.41) * mm});
            skLineSegment(sketch, "E35.4.0.6", {"start": v(1195.1, 1704.33) * mm, "end": v(1231.11, 1734.55) * mm});
            skLineSegment(sketch, "E35.4.0.7", {"start": v(895.1, 1704.33) * mm, "end": v(931.11, 1734.55) * mm});
            skLineSegment(sketch, "E35.4.0.8", {"start": v(1185, 1734.55) * mm, "end": v(1146.7, 1702.41) * mm});
            skLineSegment(sketch, "E35.4.0.9", {"start": v(1035, 1734.55) * mm, "end": v(996.7, 1702.41) * mm});
            skLineSegment(sketch, "E35.4.0.10", {"start": v(1045.1, 1704.33) * mm, "end": v(1081.11, 1734.55) * mm});
            skLineSegment(sketch, "E35.4.0.11", {"start": v(1245.1, 1704.33) * mm, "end": v(1281.11, 1734.55) * mm});
            skLineSegment(sketch, "E35.4.0.12", {"start": v(995.1, 1704.33) * mm, "end": v(1031.11, 1734.55) * mm});
            skLineSegment(sketch, "E35.4.0.13", {"start": v(1095.1, 1704.33) * mm, "end": v(1131.11, 1734.55) * mm});
            skLineSegment(sketch, "E35.4.0.14", {"start": v(1346.7, 1702.41) * mm, "end": v(1296.7, 1702.41) * mm, "construction": true});
            skLineSegment(sketch, "E35.4.0.15", {"start": v(985, 1734.55) * mm, "end": v(946.7, 1702.41) * mm});
            skLineSegment(sketch, "E35.4.0.16", {"start": v(1145.1, 1704.33) * mm, "end": v(1181.11, 1734.55) * mm});
            skLineSegment(sketch, "E35.4.0.17", {"start": v(1295.1, 1704.33) * mm, "end": v(1331.11, 1734.55) * mm});
            skLineSegment(sketch, "E35.4.0.18", {"start": v(1345.1, 1704.33) * mm, "end": v(1381.11, 1734.55) * mm});
            skLineSegment(sketch, "E35.4.0.19", {"start": v(1385, 1734.55) * mm, "end": v(1346.7, 1702.41) * mm});
            skLineSegment(sketch, "E35.4.0.20", {"start": v(1335, 1734.55) * mm, "end": v(1296.7, 1702.41) * mm});
            skLineSegment(sketch, "E35.4.0.21", {"start": v(996.7, 1702.41) * mm, "end": v(995.1, 1704.33) * mm});
            skLineSegment(sketch, "E35.4.0.22", {"start": v(931.11, 1734.55) * mm, "end": v(935, 1734.55) * mm});
            skLineSegment(sketch, "E35.4.0.23", {"start": v(1381.11, 1734.55) * mm, "end": v(1385, 1734.55) * mm});
            skLineSegment(sketch, "E35.4.0.24", {"start": v(1281.11, 1734.55) * mm, "end": v(1285, 1734.55) * mm});
            skLineSegment(sketch, "E35.4.0.25", {"start": v(946.7, 1702.41) * mm, "end": v(945.1, 1704.33) * mm});
            skLineSegment(sketch, "E35.4.0.26", {"start": v(1181.11, 1734.55) * mm, "end": v(1185, 1734.55) * mm});
            skLineSegment(sketch, "E35.4.0.27", {"start": v(1331.11, 1734.55) * mm, "end": v(1335, 1734.55) * mm});
            skLineSegment(sketch, "E35.4.0.28", {"start": v(1031.11, 1734.55) * mm, "end": v(1035, 1734.55) * mm});
            skLineSegment(sketch, "E35.4.0.29", {"start": v(1046.7, 1702.41) * mm, "end": v(1045.1, 1704.33) * mm});
            skLineSegment(sketch, "E35.4.0.30", {"start": v(981.11, 1734.55) * mm, "end": v(985, 1734.55) * mm});
            skLineSegment(sketch, "E35.4.0.31", {"start": v(896.7, 1702.41) * mm, "end": v(895.1, 1704.33) * mm});
            skLineSegment(sketch, "E35.4.0.32", {"start": v(1096.7, 1702.41) * mm, "end": v(1095.1, 1704.33) * mm});
            skLineSegment(sketch, "E35.4.0.33", {"start": v(1131.11, 1734.55) * mm, "end": v(1135, 1734.55) * mm});
            skLineSegment(sketch, "E35.4.0.34", {"start": v(1081.11, 1734.55) * mm, "end": v(1085, 1734.55) * mm});
            skLineSegment(sketch, "E35.4.0.35", {"start": v(1346.7, 1702.41) * mm, "end": v(1345.1, 1704.33) * mm});
            skLineSegment(sketch, "E35.4.0.36", {"start": v(1296.7, 1702.41) * mm, "end": v(1295.1, 1704.33) * mm});
            skLineSegment(sketch, "E35.4.0.37", {"start": v(1231.11, 1734.55) * mm, "end": v(1235, 1734.55) * mm});
            skLineSegment(sketch, "E35.4.0.38", {"start": v(1196.7, 1702.41) * mm, "end": v(1195.1, 1704.33) * mm});
            skLineSegment(sketch, "E35.4.0.39", {"start": v(1146.7, 1702.41) * mm, "end": v(1145.1, 1704.33) * mm});
            skLineSegment(sketch, "E35.4.0.40", {"start": v(1246.7, 1702.41) * mm, "end": v(1245.1, 1704.33) * mm});
            skLineSegment(sketch, "E35.5.0.0", {"start": v(765, 1734.55) * mm, "end": v(726.7, 1702.41) * mm});
            skLineSegment(sketch, "E35.5.0.1", {"start": v(565, 1734.55) * mm, "end": v(526.7, 1702.41) * mm});
            skLineSegment(sketch, "E35.5.0.2", {"start": v(425.1, 1704.33) * mm, "end": v(461.11, 1734.55) * mm});
            skLineSegment(sketch, "E35.5.0.3", {"start": v(715, 1734.55) * mm, "end": v(676.7, 1702.41) * mm});
            skLineSegment(sketch, "E35.5.0.4", {"start": v(615, 1734.55) * mm, "end": v(576.7, 1702.41) * mm});
            skLineSegment(sketch, "E35.5.0.5", {"start": v(415, 1734.55) * mm, "end": v(376.7, 1702.41) * mm});
            skLineSegment(sketch, "E35.5.0.6", {"start": v(675.1, 1704.33) * mm, "end": v(711.11, 1734.55) * mm});
            skLineSegment(sketch, "E35.5.0.7", {"start": v(375.1, 1704.33) * mm, "end": v(411.11, 1734.55) * mm});
            skLineSegment(sketch, "E35.5.0.8", {"start": v(665, 1734.55) * mm, "end": v(626.7, 1702.41) * mm});
            skLineSegment(sketch, "E35.5.0.9", {"start": v(515, 1734.55) * mm, "end": v(476.7, 1702.41) * mm});
            skLineSegment(sketch, "E35.5.0.10", {"start": v(525.1, 1704.33) * mm, "end": v(561.11, 1734.55) * mm});
            skLineSegment(sketch, "E35.5.0.11", {"start": v(725.1, 1704.33) * mm, "end": v(761.11, 1734.55) * mm});
            skLineSegment(sketch, "E35.5.0.12", {"start": v(475.1, 1704.33) * mm, "end": v(511.11, 1734.55) * mm});
            skLineSegment(sketch, "E35.5.0.13", {"start": v(575.1, 1704.33) * mm, "end": v(611.11, 1734.55) * mm});
            skLineSegment(sketch, "E35.5.0.14", {"start": v(826.7, 1702.41) * mm, "end": v(776.7, 1702.41) * mm, "construction": true});
            skLineSegment(sketch, "E35.5.0.15", {"start": v(465, 1734.55) * mm, "end": v(426.7, 1702.41) * mm});
            skLineSegment(sketch, "E35.5.0.16", {"start": v(625.1, 1704.33) * mm, "end": v(661.11, 1734.55) * mm});
            skLineSegment(sketch, "E35.5.0.17", {"start": v(775.1, 1704.33) * mm, "end": v(811.11, 1734.55) * mm});
            skLineSegment(sketch, "E35.5.0.18", {"start": v(825.1, 1704.33) * mm, "end": v(861.11, 1734.55) * mm});
            skLineSegment(sketch, "E35.5.0.19", {"start": v(865, 1734.55) * mm, "end": v(826.7, 1702.41) * mm});
            skLineSegment(sketch, "E35.5.0.20", {"start": v(815, 1734.55) * mm, "end": v(776.7, 1702.41) * mm});
            skLineSegment(sketch, "E35.5.0.21", {"start": v(476.7, 1702.41) * mm, "end": v(475.1, 1704.33) * mm});
            skLineSegment(sketch, "E35.5.0.22", {"start": v(411.11, 1734.55) * mm, "end": v(415, 1734.55) * mm});
            skLineSegment(sketch, "E35.5.0.23", {"start": v(861.11, 1734.55) * mm, "end": v(865, 1734.55) * mm});
            skLineSegment(sketch, "E35.5.0.24", {"start": v(761.11, 1734.55) * mm, "end": v(765, 1734.55) * mm});
            skLineSegment(sketch, "E35.5.0.25", {"start": v(426.7, 1702.41) * mm, "end": v(425.1, 1704.33) * mm});
            skLineSegment(sketch, "E35.5.0.26", {"start": v(661.11, 1734.55) * mm, "end": v(665, 1734.55) * mm});
            skLineSegment(sketch, "E35.5.0.27", {"start": v(811.11, 1734.55) * mm, "end": v(815, 1734.55) * mm});
            skLineSegment(sketch, "E35.5.0.28", {"start": v(511.11, 1734.55) * mm, "end": v(515, 1734.55) * mm});
            skLineSegment(sketch, "E35.5.0.29", {"start": v(526.7, 1702.41) * mm, "end": v(525.1, 1704.33) * mm});
            skLineSegment(sketch, "E35.5.0.30", {"start": v(461.11, 1734.55) * mm, "end": v(465, 1734.55) * mm});
            skLineSegment(sketch, "E35.5.0.31", {"start": v(376.7, 1702.41) * mm, "end": v(375.1, 1704.33) * mm});
            skLineSegment(sketch, "E35.5.0.32", {"start": v(576.7, 1702.41) * mm, "end": v(575.1, 1704.33) * mm});
            skLineSegment(sketch, "E35.5.0.33", {"start": v(611.11, 1734.55) * mm, "end": v(615, 1734.55) * mm});
            skLineSegment(sketch, "E35.5.0.34", {"start": v(561.11, 1734.55) * mm, "end": v(565, 1734.55) * mm});
            skLineSegment(sketch, "E35.5.0.35", {"start": v(826.7, 1702.41) * mm, "end": v(825.1, 1704.33) * mm});
            skLineSegment(sketch, "E35.5.0.36", {"start": v(776.7, 1702.41) * mm, "end": v(775.1, 1704.33) * mm});
            skLineSegment(sketch, "E35.5.0.37", {"start": v(711.11, 1734.55) * mm, "end": v(715, 1734.55) * mm});
            skLineSegment(sketch, "E35.5.0.38", {"start": v(676.7, 1702.41) * mm, "end": v(675.1, 1704.33) * mm});
            skLineSegment(sketch, "E35.5.0.39", {"start": v(626.7, 1702.41) * mm, "end": v(625.1, 1704.33) * mm});
            skLineSegment(sketch, "E35.5.0.40", {"start": v(726.7, 1702.41) * mm, "end": v(725.1, 1704.33) * mm});
            skLineSegment(sketch, "E35.direction1", {"start": v(2976.7, 1702.41) * mm, "end": v(2456.7, 1702.41) * mm, "construction": true});
            skSolve(sketch);
        }
        {
            var Q0;
            Q0 = qSketchRegion(id + "F18", true);
            var Q1;
            Q1=makeQuery(id+"F15.boolean.opBoolean","COPY",FACE,{"derivedFrom":makeQuery(id+"F15.opExtrude","SWEPT_FACE",FACE,{"disambiguationData":[OSD([sQuery(id+"F14.wireOp",EDGE,"E23.bottom")])]})});
            extrude(context, id + "F19", {"entities" : qUnion([Q0]), "operationType" : NewBodyOperationType.ADD, "endBound" : BoundingType.UP_TO_SURFACE, "depth" : 25 * mm, "endBoundEntityFace" : qUnion([Q1]), "offsetDistance" : 25 * mm});
        }
    });
